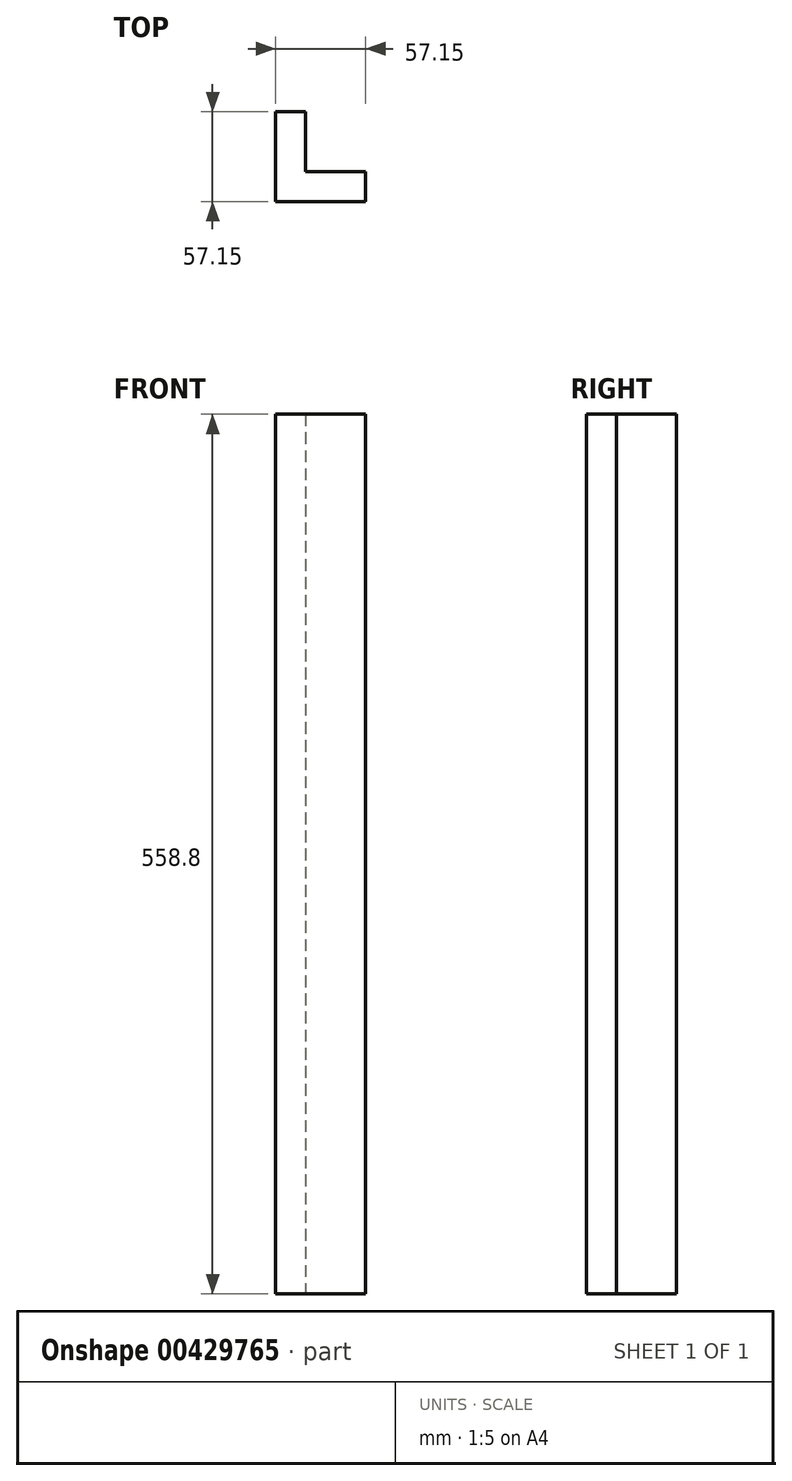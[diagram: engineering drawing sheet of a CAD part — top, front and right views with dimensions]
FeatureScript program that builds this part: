
annotation { "Feature Type Name" : "Feature", "Feature Type Description" : "" }
export const myFeature = defineFeature(function(context is Context, id is Id, definition is map)
    precondition{}
    {
        {
            var Q0;
            Q0=qCreatedBy(makeId("Top.planeOp"),FACE);
            var sketch = newSketch(context, id + "F0", { "sketchPlane" : qUnion([Q0])});
            skLineSegment(sketch, "E0", {"start": v(0, 0) * mm, "end": v(0, 57.15) * mm});
            skLineSegment(sketch, "E1", {"start": v(0, 57.15) * mm, "end": v(19.05, 57.15) * mm});
            skLineSegment(sketch, "E2", {"start": v(19.05, 57.15) * mm, "end": v(19.05, 19.05) * mm});
            skLineSegment(sketch, "E3", {"start": v(19.05, 19.05) * mm, "end": v(57.15, 19.05) * mm});
            skLineSegment(sketch, "E4", {"start": v(57.15, 19.05) * mm, "end": v(57.15, 0) * mm});
            skLineSegment(sketch, "E5", {"start": v(57.15, 0) * mm, "end": v(0, 0) * mm});
            skSolve(sketch);
        }
        {
            var Q0;
            Q0 = qSketchRegion(id + "F0", true);
            extrude(context, id + "F1", {"entities" : qUnion([Q0]), "depth" : 558.8 * mm});
        }
    });
